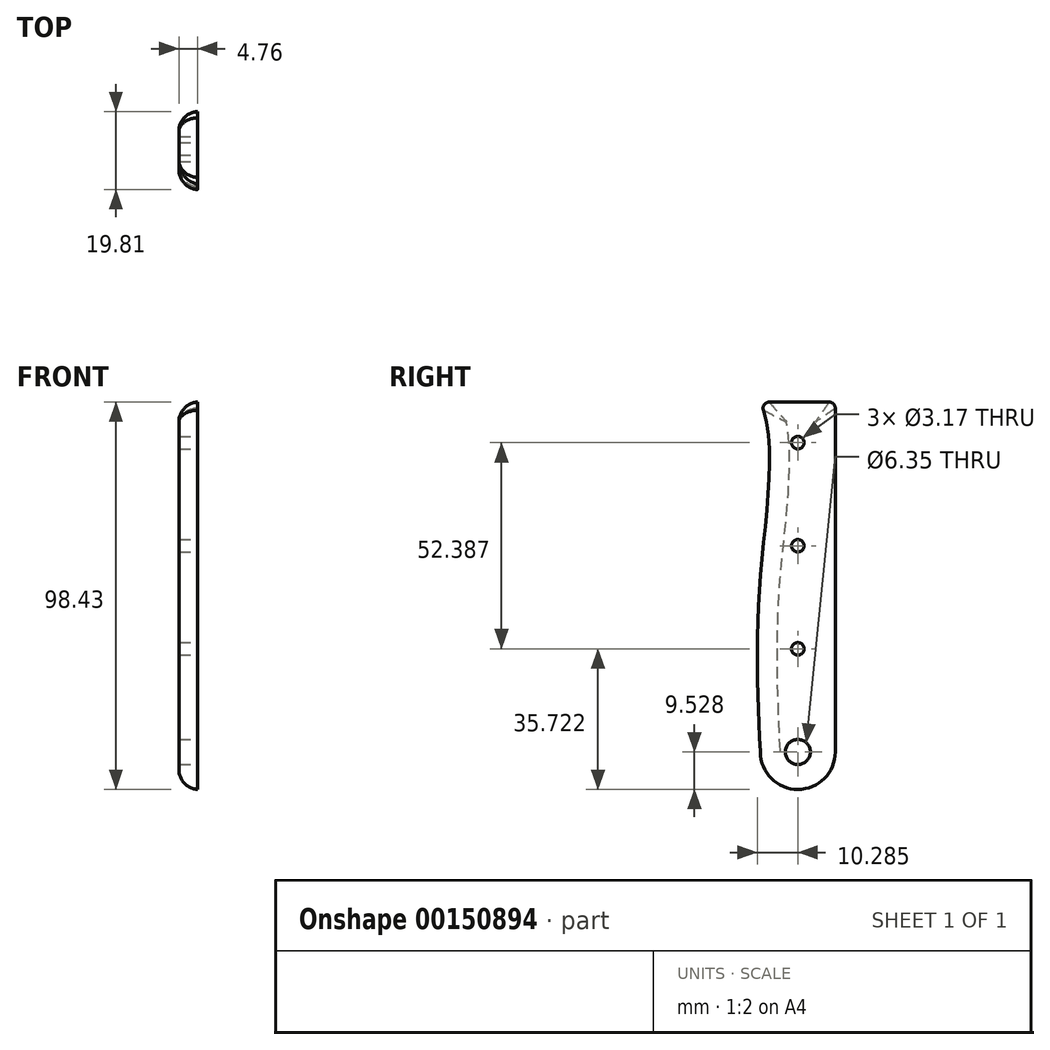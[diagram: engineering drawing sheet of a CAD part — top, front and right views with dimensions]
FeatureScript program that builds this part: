
annotation { "Feature Type Name" : "Feature", "Feature Type Description" : "" }
export const myFeature = defineFeature(function(context is Context, id is Id, definition is map)
    precondition{}
    {
        {
            var Q0;
            Q0=qCreatedBy(makeId("Right.planeOp"),FACE);
            var sketch = newSketch(context, id + "F0", { "sketchPlane" : qUnion([Q0])});
            skLineSegment(sketch, "E0", {"start": v(11.54, -116.33) * mm, "end": v(11.54, -2.03) * mm, "construction": true});
            skPoint(sketch, "E1", {"position": v(-7.5, -116.33) * mm});
            skPoint(sketch, "E2", {"position": v(2.02, -116.33) * mm});
            skPoint(sketch, "E3", {"position": v(2.02, -106.8) * mm});
            skLineSegment(sketch, "E4", {"start": v(-7.5, -106.8) * mm, "end": v(11.54, -106.8) * mm, "construction": true});
            skArc(sketch, "E5", {"start": v(-7.5, -106.8) * mm, "mid": v(2.02, -116.33) * mm, "end": v(11.54, -106.8) * mm});
            skLineSegment(sketch, "E6", {"start": v(11.54, -2.03) * mm, "end": v(11.54, -106.8) * mm, "construction": true});
            skPoint(sketch, "E7", {"position": v(-7.5, -17.9) * mm});
            skLineSegment(sketch, "E8", {"start": v(11.54, -2.03) * mm, "end": v(-26.56, -2.03) * mm});
            skLineSegment(sketch, "E9", {"start": v(2.02, -106.8) * mm, "end": v(2.02, -2.03) * mm, "construction": true});
            skPoint(sketch, "E10", {"position": v(-7.5, -62.35) * mm});
            skFitSpline(sketch, "E11", {"points": [v(-26.56, -2.03) * mm, v(-7.5, -17.9) * mm, v(-7.5, -62.35) * mm, v(-7.5, -106.8) * mm], "startDerivative": vector(86.2, -43.71) * mm, "endDerivative": vector(5.4, -117.19) * mm});
            skPoint(sketch, "E12", {"position": v(8.37, -2.03) * mm});
            skPoint(sketch, "E13", {"position": v(11.54, -17.9) * mm});
            skPoint(sketch, "E14", {"position": v(11.54, 13.85) * mm});
            skArc(sketch, "E15", {"start": v(11.54, 13.85) * mm, "mid": v(8.37, -2.03) * mm, "end": v(11.54, -17.9) * mm});
            skLineSegment(sketch, "E16", {"start": v(11.54, -17.9) * mm, "end": v(11.54, -106.8) * mm});
            skLineSegment(sketch, "E17", {"start": v(-26.56, 340.87) * mm, "end": v(11.54, 264.67) * mm});
            skPoint(sketch, "E18", {"position": v(11.54, 340.87) * mm});
            skLineSegment(sketch, "E19", {"start": v(11.54, 264.67) * mm, "end": v(11.54, 13.85) * mm});
            skLineSegment(sketch, "E20", {"start": v(-26.56, 340.87) * mm, "end": v(-26.56, -2.03) * mm});
            skPoint(sketch, "E21", {"position": v(2.02, -54.41) * mm});
            skPoint(sketch, "E22", {"position": v(2.02, -28.22) * mm});
            skPoint(sketch, "E23", {"position": v(2.02, -80.6) * mm});
            skPoint(sketch, "E24", {"position": v(-13.86, -2.03) * mm});
            skPoint(sketch, "E25", {"position": v(-13.86, -9.67) * mm});
            skLineSegment(sketch, "E26", {"start": v(-13.86, -9.67) * mm, "end": v(-13.86, 315.47) * mm});
            skLineSegment(sketch, "E27", {"start": v(11.54, -17.9) * mm, "end": v(-7.5, -17.9) * mm});
            skSolve(sketch);
        }
        {
            var Q0;
            {var subQ5=sQuery(id+"F0.wireOp",EDGE,"E5");Q0=makeQuery(id+"F0.imprint","IMPRINT",FACE,{"disambiguationData":[TD([[makeQuery(id+"F0.imprint","IMPRINT",EDGE,{"derivedFrom":subQ5}),1.0]])]});}
            extrude(context, id + "F1", {"entities" : qUnion([Q0]), "oppositeDirection" : true, "depth" : 4.76 * mm});
        }
        {
            var Q0;
            Q0=sQuery(id+"F0.wireOp",VERTEX,"E22");
            var Q1;
            Q1=sQuery(id+"F0.wireOp",VERTEX,"E21");
            var Q2;
            Q2=sQuery(id+"F0.wireOp",VERTEX,"E23");
            var Q3;
            Q3=makeQuery(id+"F1.opExtrude","SWEPT_BODY",BODY,{"disambiguationData":[OSD([sQuery(id+"F0.wireOp",EDGE,"E5"),sQuery(id+"F0.wireOp",EDGE,"E8"),sQuery(id+"F0.wireOp",EDGE,"E11"),sQuery(id+"F0.wireOp",EDGE,"E15"),sQuery(id+"F0.wireOp",EDGE,"E16")])]});
            hole(context, id + "F4", {"style" : HoleStyle.SIMPLE, "endStyle" : HoleEndStyle.THROUGH, "holeDiameter" : 3.17 * mm, "locations" : qUnion([Q0, Q1, Q2]), "scope" : qUnion([Q3]), "isTappedThrough" : true});
        }
        {
            var Q0;
            Q0=sQuery(id+"F0.wireOp",VERTEX,"E3");
            var Q1;
            Q1=makeQuery(id+"F1.opExtrude","SWEPT_BODY",BODY,{"disambiguationData":[OSD([sQuery(id+"F0.wireOp",EDGE,"E5"),sQuery(id+"F0.wireOp",EDGE,"E8"),sQuery(id+"F0.wireOp",EDGE,"E11"),sQuery(id+"F0.wireOp",EDGE,"E15"),sQuery(id+"F0.wireOp",EDGE,"E16")])]});
            hole(context, id + "F2", {"style" : HoleStyle.SIMPLE, "endStyle" : HoleEndStyle.THROUGH, "holeDiameter" : 6.35 * mm, "locations" : qUnion([Q0]), "scope" : qUnion([Q1]), "isTappedThrough" : true});
        }
        {
            var Q0;
            Q0=makeQuery(id+"F1.opExtrude","SWEPT_EDGE",EDGE,{"disambiguationData":[OSD([sQuery(id+"F0.wireOp",EDGE,"E8"),sQuery(id+"F0.wireOp",EDGE,"E15")])]});
            var Q1;
            Q1=makeQuery(id+"F1.opExtrude","SWEPT_EDGE",EDGE,{"disambiguationData":[OSD([sQuery(id+"F0.wireOp",EDGE,"E8"),sQuery(id+"F0.wireOp",EDGE,"E11"),sQuery(id+"F0.wireOp",EDGE,"E20")])]});
            fillet(context, id + "F5", {"entities" : qUnion([Q0, Q1]), "radius" : 1.59 * mm, "tangentPropagation" : true, "allowEdgeOverflow" : false});
        }
        {
            var Q0;
            Q0=makeQuery(id+"F1.opExtrude","CAP_EDGE",EDGE,{"disambiguationData":[OSD([sQuery(id+"F0.wireOp",EDGE,"E8")])],"isStart":false});
            var Q1;
            Q1=makeQuery(id+"F1.opExtrude","CAP_EDGE",EDGE,{"disambiguationData":[OSD([sQuery(id+"F0.wireOp",EDGE,"E11")])],"isStart":false});
            var Q2;
            Q2=makeQuery(id+"F1.opExtrude","CAP_EDGE",EDGE,{"disambiguationData":[OSD([sQuery(id+"F0.wireOp",EDGE,"E5")])],"isStart":false});
            var Q3;
            Q3=makeQuery(id+"F1.opExtrude","CAP_EDGE",EDGE,{"disambiguationData":[OSD([sQuery(id+"F0.wireOp",EDGE,"E16")])],"isStart":false});
            fillet(context, id + "F3", {"entities" : qUnion([Q0, Q1, Q2, Q3]), "radius" : 5.08 * mm, "tangentPropagation" : true, "allowEdgeOverflow" : false});
        }
    });
